# Revit family: 5abd313ca3195bb7c46b99cf50d73354a2686976_new
name_source: partatom
category: Columns
revit_build: Autodesk Revit 2018 (Build: 20170421_2315(x64)
units: mm (PartAtom-declared; Revit-internal decimal feet)

## family parameters
Automatically joins geometry to walls = Yes
Cut with Voids When Loaded = No
OmniClass Number = 23.25.30.11.14.11
OmniClass Title = Columns
Shared = No
Show family pre-cut in plan views = Yes

## types (3) — shared parameters
Apparent Power - Electrical = 0 VA
Assembly Code = B1010200
Electrical Potential - Electrical = 0 V
Force -  Structural = 0.00 kip
Line Spring Coefficient - Structural = 0.0 kip/ft²
Linear Force - Structural = 0.000 kip/ft
Linear Moment - Structural = 0.00 kip-ft/ft
Material = <By Category>
Moment - Structural = 0.00 kip-ft
Number of Poles - Electrical = 1
Point Spring Coefficient - Structural = 0.0 kip/in
Power - Electrical = 0 W
Rotational Line Spring Coefficient - Structural = 0.0 kip-ft/°/ft
Rotational Point Spring Coefficient - Structural = 0.0 kip-ft/°
Stress - Structural = 0.00 ksi
Wattage - Electrical = 0 W

## per-type parameters (varying)
- 24" x 24": Acceleration - Structural=0.0 ft/s²; Area Force - Structural=0.0000 ksf; Area Spring Coefficient - Structural=0.0 kip/ft³; Bar Diameter - Structural=0' - 0"; Cable Tray Size - Electrical=0"; Chamfer=0' - 4"; Color Temperature - Electrical=0 K; Conduit Size - Electrical=0"; Crack Width - Structural=0.00"; Current - Electrical=0 A; Demand Factor - Electrical=0.00%; Depth=2' - 0"; Displacement/Deflection - Structural=0.00"; Efficacy - Electrical=0 lm/W; Electrical Resistivity - Electrical=0.0000 ohm·m; Frequency - Electrical=0 Hz; Frequency - Structural=0.0 Hz; Illuminance - Electrical=0 lx; Luminance - Electrical=0 cd/m²; Luminous Flux - Electrical=0 lm; Luminous Intensity - Electrical=0 cd; Mass - Structural=0.00 lbm; Mass per Unit Area - Structural=0.00 lb/ft²; Mass per Unit Length - Structural=0.00 lb/ft; Moment of Inertia - Structural=0.00 in4; Offset Base=0' - 0"; Offset Top=0' - 0"; Period - Structural=0.0 s; Power Density - Electrical=0.00 W/ft²; Pulsation - Structural=0.0 rad/s; Reinforcement Area - Structural=0.00 in²; Reinforcement Area per Unit Length=0.00 in²/ft; Reinforcement Cover - Structural=0' - 0"; Reinforcement Length - Structural=0' - 0"; Reinforcement Spacing - Structural=0' - 0"; Reinforcement Volume - Structural=0.00 in³; Rotation - Structural=0.000 rad; Section Dimension - Structural=0' - 0"; Section Modulus - Structural=0.00 in³; Section Property - Structural=0.000"; Surface Area per Unit Length - Structural=0.00 ft²/ft; Temperature - Electrical=-1287 °F; Temperature Difference - Electrical=0 °F; Thermal Expansion Coefficient - Structural=0.00000 1/°F; Unit Weight - Structural=0.00 lb/ft³; Velocity - Structural=0.0 ft/s; Warping Constant - Structural=0.00 in6; Weight - Structural=0.00 lbf; Weight per Unit Length - Structural=0.00 lbf/ft; Width=2' - 0"; Wire Diameter - Electrical=0.000000"
- 18" x 24": Acceleration - Structural=0.0 ft/s²; Area Force - Structural=0.0000 ksf; Area Spring Coefficient - Structural=0.0 kip/ft³; Bar Diameter - Structural=0' - 0"; Cable Tray Size - Electrical=0"; Chamfer=0' - 2"; Color Temperature - Electrical=0 K; Conduit Size - Electrical=0"; Crack Width - Structural=0.00"; Current - Electrical=0 A; Demand Factor - Electrical=0.00%; Depth=1' - 6"; Displacement/Deflection - Structural=0.00"; Efficacy - Electrical=0 lm/W; Electrical Resistivity - Electrical=0.0000 ohm·m; Frequency - Electrical=0 Hz; Frequency - Structural=0.0 Hz; Illuminance - Electrical=0 lx; Luminance - Electrical=0 cd/m²; Luminous Flux - Electrical=0 lm; Luminous Intensity - Electrical=0 cd; Mass - Structural=0.00 lbm; Mass per Unit Area - Structural=0.00 lb/ft²; Mass per Unit Length - Structural=0.00 lb/ft; Moment of Inertia - Structural=0.00 in4; Offset Base=0' - 0"; Offset Top=0' - 0"; Period - Structural=0.0 s; Power Density - Electrical=0.00 W/ft²; Pulsation - Structural=0.0 rad/s; Reinforcement Area - Structural=0.00 in²; Reinforcement Area per Unit Length=0.00 in²/ft; Reinforcement Cover - Structural=0' - 0"; Reinforcement Length - Structural=0' - 0"; Reinforcement Spacing - Structural=0' - 0"; Reinforcement Volume - Structural=0.00 in³; Rotation - Structural=0.000 rad; Section Dimension - Structural=0' - 0"; Section Modulus - Structural=0.00 in³; Section Property - Structural=0.000"; Surface Area per Unit Length - Structural=0.00 ft²/ft; Temperature - Electrical=-1287 °F; Temperature Difference - Electrical=0 °F; Thermal Expansion Coefficient - Structural=0.00000 1/°F; Unit Weight - Structural=0.00 lb/ft³; Velocity - Structural=0.0 ft/s; Warping Constant - Structural=0.00 in6; Weight - Structural=0.00 lbf; Weight per Unit Length - Structural=0.00 lbf/ft; Width=2' - 0"; Wire Diameter - Electrical=0.000000"
- 18" x 18": Acceleration - Structural=1.0 ft/s²; Area Force - Structural=0.0001 ksf; Area Spring Coefficient - Structural=1.0 kip/ft³; Bar Diameter - Structural=1' - 0"; Cable Tray Size - Electrical=12"; Chamfer=0' - 6"; Color Temperature - Electrical=1 K; Conduit Size - Electrical=12"; Crack Width - Structural=12.00"; Current - Electrical=1 A; Demand Factor - Electrical=100.00%; Depth=2' - 2"; Displacement/Deflection - Structural=12.00"; Efficacy - Electrical=11 lm/W; Electrical Resistivity - Electrical=0.0283 ohm·m; Frequency - Electrical=1 Hz; Frequency - Structural=1.0 Hz; Illuminance - Electrical=11 lx; Load Classification=Lighting; Luminance - Electrical=11 cd/m²; Luminous Flux - Electrical=1 lm; Luminous Intensity - Electrical=1 cd; Mass - Structural=2.20 lbm; Mass per Unit Area - Structural=2.20 lb/ft²; Mass per Unit Length - Structural=2.20 lb/ft; Moment of Inertia - Structural=20736.00 in4; Offset Base=0' - 6"; Offset Top=0' - 6"; Period - Structural=1.0 s; Power Density - Electrical=0.09 W/ft²; Pulsation - Structural=1.0 rad/s; Reinforcement Area - Structural=144.00 in²; Reinforcement Area per Unit Length=144.00 in²/ft; Reinforcement Cover - Structural=1' - 0"; Reinforcement Length - Structural=1' - 0"; Reinforcement Spacing - Structural=1' - 0"; Reinforcement Volume - Structural=1728.00 in³; Rotation - Structural=1.000 rad; Section Dimension - Structural=1' - 0"; Section Modulus - Structural=1728.00 in³; Section Property - Structural=12.000"; Surface Area per Unit Length - Structural=1.00 ft²/ft; Temperature - Electrical=-458 °F; Temperature Difference - Electrical=2 °F; Thermal Expansion Coefficient - Structural=0.55556 1/°F; Unit Weight - Structural=0.07 lb/ft³; Velocity - Structural=1.0 ft/s; Warping Constant - Structural=2985984.00 in6; Weight - Structural=0.07 lbf; Weight per Unit Length - Structural=0.07 lbf/ft; Width=2' - 2"; Wire Diameter - Electrical=12.000000"

## geometry (parser evidence)
native form markers: Sweep x1
no freeform markers — native parametric forms only
